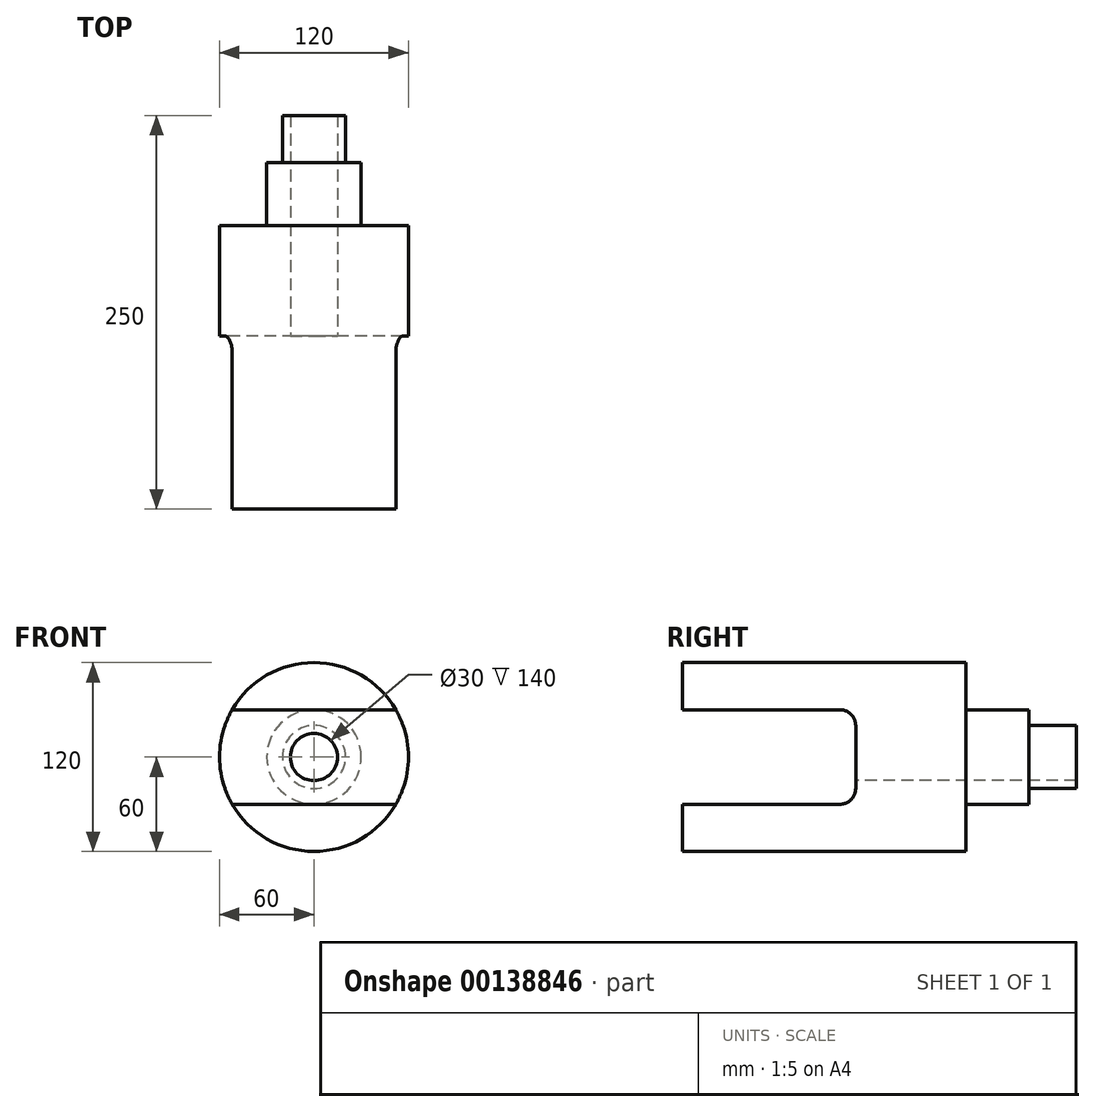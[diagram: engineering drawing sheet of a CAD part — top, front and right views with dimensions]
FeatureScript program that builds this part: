
annotation { "Feature Type Name" : "Feature", "Feature Type Description" : "" }
export const myFeature = defineFeature(function(context is Context, id is Id, definition is map)
    precondition{}
    {
        {
            var Q0;
            Q0=qCreatedBy(makeId("Front.planeOp"),FACE);
            var sketch = newSketch(context, id + "F0", { "sketchPlane" : qUnion([Q0])});
            skCircle(sketch, "E0", {"center": v(0, 0) * mm, "radius": 20 * mm});
            skSolve(sketch);
        }
        {
            var Q0;
            Q0 = qSketchRegion(id + "F0", true);
            extrude(context, id + "F1", {"entities" : qUnion([Q0]), "depth" : 30 * mm});
        }
        {
            var Q0;
            Q0=makeQuery(id+"F1.opExtrude","CAP_FACE",FACE,{"disambiguationData":[OSD([sQuery(id+"F0.wireOp",EDGE,"E0")])],"isStart":false});
            var sketch = newSketch(context, id + "F2", { "sketchPlane" : qUnion([Q0])});
            skCircle(sketch, "E1", {"center": v(0, 0) * mm, "radius": 30 * mm});
            skSolve(sketch);
        }
        {
            var Q0;
            Q0 = qSketchRegion(id + "F2", true);
            extrude(context, id + "F3", {"entities" : qUnion([Q0]), "operationType" : NewBodyOperationType.ADD, "depth" : 40 * mm});
        }
        {
            var Q0;
            Q0=makeQuery(id+"F3.opExtrude","CAP_FACE",FACE,{"disambiguationData":[OSD([sQuery(id+"F2.wireOp",EDGE,"E1")])],"isStart":false});
            var sketch = newSketch(context, id + "F4", { "sketchPlane" : qUnion([Q0])});
            skCircle(sketch, "E2", {"center": v(0, 0) * mm, "radius": 60 * mm});
            skSolve(sketch);
        }
        {
            var Q0;
            Q0 = qSketchRegion(id + "F4", true);
            extrude(context, id + "F5", {"entities" : qUnion([Q0]), "operationType" : NewBodyOperationType.ADD, "depth" : 180 * mm});
        }
        {
            var Q0;
            Q0=makeQuery(id+"F5.opExtrude","CAP_FACE",FACE,{"disambiguationData":[OSD([sQuery(id+"F4.wireOp",EDGE,"E2")])],"isStart":false});
            var sketch = newSketch(context, id + "F6", { "sketchPlane" : qUnion([Q0])});
            skCircle(sketch, "E3", {"center": v(0, 0) * mm, "radius": 15 * mm});
            skSolve(sketch);
        }
        {
            var Q0;
            Q0 = qSketchRegion(id + "F6", true);
            extrude(context, id + "F7", {"entities" : qUnion([Q0]), "operationType" : NewBodyOperationType.REMOVE, "oppositeDirection" : true, "depth" : 250 * mm});
        }
        {
            var Q0;
            Q0=makeQuery(id+"F5.opExtrude","CAP_FACE",FACE,{"disambiguationData":[OSD([sQuery(id+"F4.wireOp",EDGE,"E2")])],"isStart":false});
            var sketch = newSketch(context, id + "F8", { "sketchPlane" : qUnion([Q0])});
            skLineSegment(sketch, "E4.bottom", {"start": v(70.68, -30) * mm, "end": v(-70.68, -30) * mm});
            skLineSegment(sketch, "E4.top", {"start": v(70.68, 30) * mm, "end": v(-70.68, 30) * mm});
            skLineSegment(sketch, "E4.left", {"start": v(70.68, -30) * mm, "end": v(70.68, 30) * mm});
            skLineSegment(sketch, "E4.right", {"start": v(-70.68, -30) * mm, "end": v(-70.68, 30) * mm});
            skPoint(sketch, "E4.middle", {"position": v(0, 0) * mm});
            skSolve(sketch);
        }
        {
            var Q0;
            Q0 = qSketchRegion(id + "F8", true);
            extrude(context, id + "F9", {"entities" : qUnion([Q0]), "operationType" : NewBodyOperationType.REMOVE, "oppositeDirection" : true, "depth" : 110 * mm});
        }
        {
            var Q0;
            Q0=makeQuery(id+"F9.boolean.opBoolean","COPY",EDGE,{"derivedFrom":makeQuery(id+"F9.opExtrude","CAP_EDGE",EDGE,{"disambiguationData":[OSD([sQuery(id+"F8.wireOp",EDGE,"E4.top")])],"isStart":false})});
            fillet(context, id + "F10", {"entities" : qUnion([Q0]), "radius" : 10 * mm, "tangentPropagation" : true, "allowEdgeOverflow" : false});
        }
        {
            var Q0;
            Q0=makeQuery(id+"F9.boolean.opBoolean","COPY",EDGE,{"derivedFrom":makeQuery(id+"F9.opExtrude","CAP_EDGE",EDGE,{"disambiguationData":[OSD([sQuery(id+"F8.wireOp",EDGE,"E4.bottom")])],"isStart":false})});
            fillet(context, id + "F11", {"entities" : qUnion([Q0]), "radius" : 10 * mm, "tangentPropagation" : true, "allowEdgeOverflow" : false});
        }
    });
